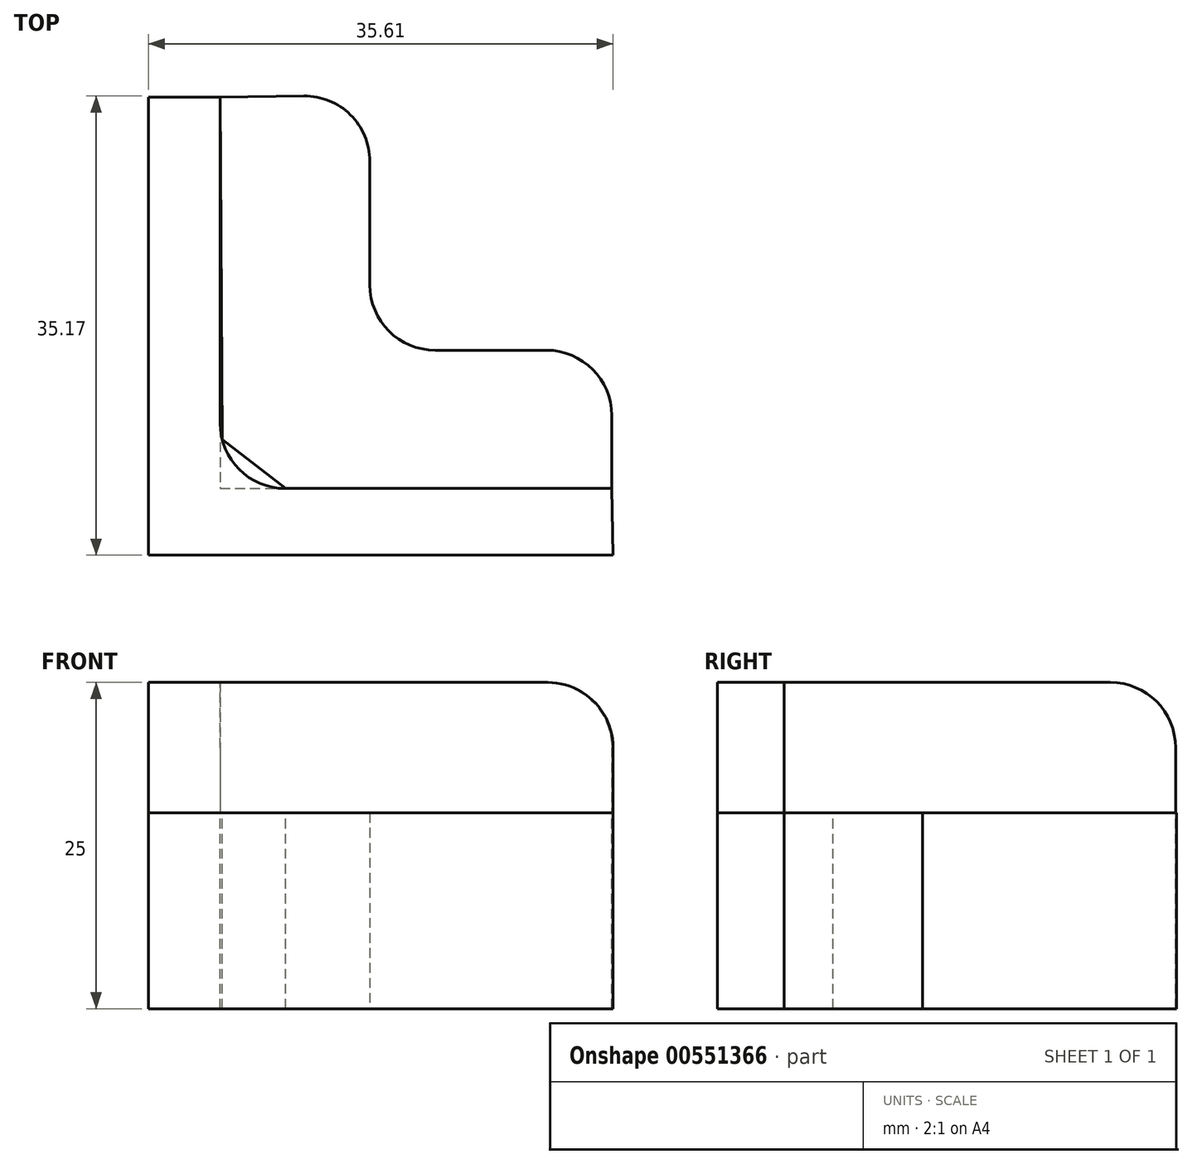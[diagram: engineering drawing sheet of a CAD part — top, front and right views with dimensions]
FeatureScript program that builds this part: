
annotation { "Feature Type Name" : "Feature", "Feature Type Description" : "" }
export const myFeature = defineFeature(function(context is Context, id is Id, definition is map)
    precondition{}
    {
        {
            var Q0;
            Q0=qCreatedBy(makeId("Top.planeOp"),FACE);
            var sketch = newSketch(context, id + "F0", { "sketchPlane" : qUnion([Q0])});
            skLineSegment(sketch, "E0", {"start": v(-15.93, 19.4) * mm, "end": v(-15.93, -10.6) * mm});
            skLineSegment(sketch, "E1", {"start": v(-15.93, -10.6) * mm, "end": v(14.07, -10.6) * mm});
            skLineSegment(sketch, "E2", {"start": v(14.07, -10.6) * mm, "end": v(14.07, 0) * mm});
            skLineSegment(sketch, "E3", {"start": v(14.07, 0) * mm, "end": v(-4.47, 0) * mm});
            skLineSegment(sketch, "E4", {"start": v(-4.47, 0) * mm, "end": v(-4.47, 19.53) * mm});
            skLineSegment(sketch, "E5", {"start": v(-4.47, 19.53) * mm, "end": v(-15.93, 19.4) * mm});
            skSolve(sketch);
        }
        {
            var Q0;
            Q0 = qSketchRegion(id + "F0", true);
            extrude(context, id + "F1", {"entities" : qUnion([Q0]), "depth" : 15 * mm, "offsetDistance" : 25 * mm});
        }
        {
            var Q0;
            Q0=makeQuery(id+"F1.opExtrude","CAP_FACE",FACE,{"disambiguationData":[OSD([sQuery(id+"F0.wireOp",EDGE,"E0"),sQuery(id+"F0.wireOp",EDGE,"E1"),sQuery(id+"F0.wireOp",EDGE,"E2"),sQuery(id+"F0.wireOp",EDGE,"E3"),sQuery(id+"F0.wireOp",EDGE,"E4"),sQuery(id+"F0.wireOp",EDGE,"E5")])],"isStart":false});
            var sketch = newSketch(context, id + "F2", { "sketchPlane" : qUnion([Q0])});
            skLineSegment(sketch, "E6", {"start": v(-15.93, 19.4) * mm, "end": v(-21.44, 19.4) * mm});
            skLineSegment(sketch, "E7", {"start": v(-21.44, 19.4) * mm, "end": v(-21.44, -15.7) * mm});
            skLineSegment(sketch, "E8", {"start": v(-21.44, -15.7) * mm, "end": v(14.17, -15.7) * mm});
            skLineSegment(sketch, "E9", {"start": v(14.17, -15.7) * mm, "end": v(14.07, -10.6) * mm});
            skLineSegment(sketch, "E10", {"start": v(14.07, -10.6) * mm, "end": v(-15.93, -10.6) * mm});
            skLineSegment(sketch, "E11", {"start": v(-15.93, -10.6) * mm, "end": v(-15.93, 19.4) * mm});
            skSolve(sketch);
        }
        {
            var Q0;
            Q0 = qSketchRegion(id + "F2", true);
            extrude(context, id + "F3", {"entities" : qUnion([Q0]), "depth" : 10 * mm, "offsetDistance" : 25 * mm});
        }
        {
            var Q0;
            Q0=makeQuery(id+"F3.opExtrude","CAP_EDGE",EDGE,{"disambiguationData":[OSD([sQuery(id+"F2.wireOp",EDGE,"E9")])],"isStart":false});
            var Q1;
            Q1=makeQuery(id+"F3.opExtrude","CAP_EDGE",EDGE,{"disambiguationData":[OSD([sQuery(id+"F2.wireOp",EDGE,"E6")])],"isStart":false});
            var Q2;
            Q2=makeQuery(id+"F1.opExtrude","SWEPT_EDGE",EDGE,{"disambiguationData":[OSD([sQuery(id+"F0.wireOp",EDGE,"E4"),sQuery(id+"F0.wireOp",EDGE,"E5")])]});
            var Q3;
            Q3=makeQuery(id+"F1.opExtrude","SWEPT_EDGE",EDGE,{"disambiguationData":[OSD([sQuery(id+"F0.wireOp",EDGE,"E2"),sQuery(id+"F0.wireOp",EDGE,"E3")])]});
            var Q4;
            Q4=makeQuery(id+"F1.opExtrude","SWEPT_EDGE",EDGE,{"disambiguationData":[OSD([sQuery(id+"F0.wireOp",EDGE,"E3"),sQuery(id+"F0.wireOp",EDGE,"E4")])]});
            var Q5;
            Q5=makeQuery(id+"F3.opExtrude","SWEPT_EDGE",EDGE,{"disambiguationData":[OSD([sQuery(id+"F2.wireOp",EDGE,"E10"),sQuery(id+"F2.wireOp",EDGE,"E11")])]});
            fillet(context, id + "F4", {"entities" : qUnion([Q0, Q1, Q2, Q3, Q4, Q5]), "radius" : 5 * mm, "tangentPropagation" : true, "allowEdgeOverflow" : false});
        }
        {
            var Q0;
            Q0=makeQuery(id+"F3.opExtrude","CAP_FACE",FACE,{"disambiguationData":[OSD([sQuery(id+"F2.wireOp",EDGE,"E6"),sQuery(id+"F2.wireOp",EDGE,"E7"),sQuery(id+"F2.wireOp",EDGE,"E8"),sQuery(id+"F2.wireOp",EDGE,"E9"),sQuery(id+"F2.wireOp",EDGE,"E10"),sQuery(id+"F2.wireOp",EDGE,"E11")])],"isStart":true});
            var sketch = newSketch(context, id + "F5", { "sketchPlane" : qUnion([Q0])});
            skLineSegment(sketch, "E12", {"start": v(-21.44, 15.7) * mm, "end": v(14.17, 15.7) * mm});
            skLineSegment(sketch, "E13", {"start": v(14.17, 15.7) * mm, "end": v(14.07, 10.6) * mm});
            skLineSegment(sketch, "E14", {"start": v(14.07, 10.6) * mm, "end": v(-10.93, 10.6) * mm});
            skLineSegment(sketch, "E15", {"start": v(-10.93, 10.6) * mm, "end": v(-15.77, 6.85) * mm});
            skLineSegment(sketch, "E16", {"start": v(-15.77, 6.85) * mm, "end": v(-15.93, -19.4) * mm});
            skLineSegment(sketch, "E17", {"start": v(-15.93, -19.4) * mm, "end": v(-21.44, -19.4) * mm});
            skLineSegment(sketch, "E18", {"start": v(-21.44, -19.4) * mm, "end": v(-21.44, 15.7) * mm});
            skSolve(sketch);
        }
        {
            var Q0;
            Q0 = qSketchRegion(id + "F5", true);
            extrude(context, id + "F6", {"entities" : qUnion([Q0]), "depth" : 15 * mm, "offsetDistance" : 25 * mm});
        }
    });
